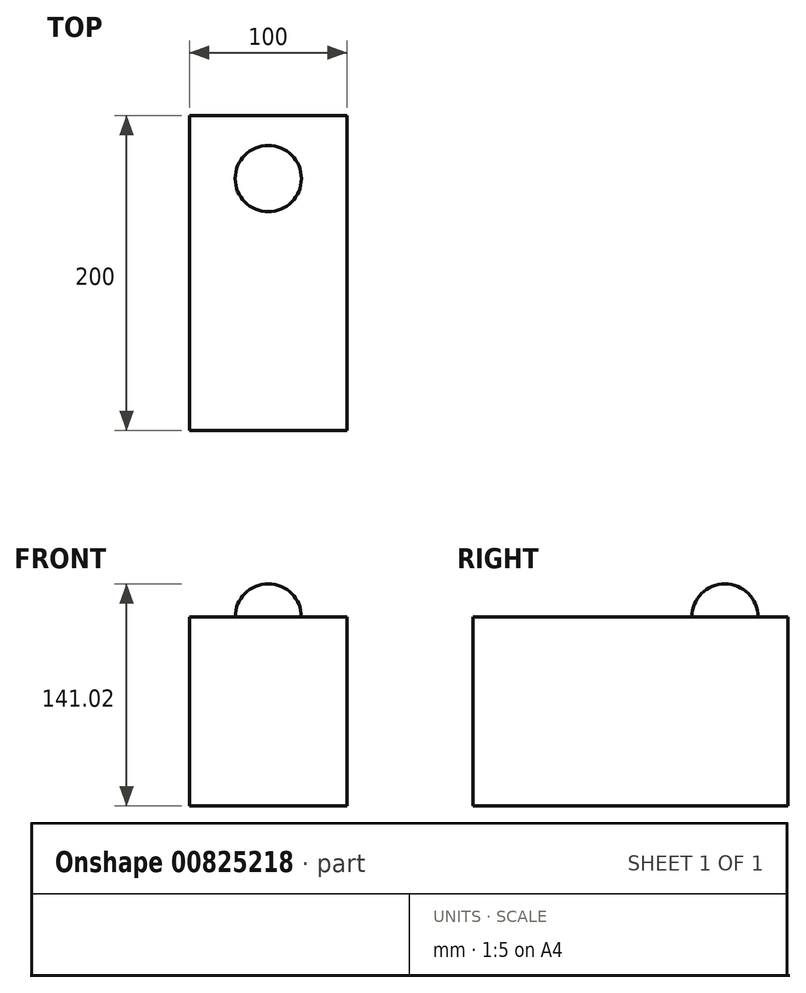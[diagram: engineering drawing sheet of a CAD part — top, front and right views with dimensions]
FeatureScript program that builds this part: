
annotation { "Feature Type Name" : "Feature", "Feature Type Description" : "" }
export const myFeature = defineFeature(function(context is Context, id is Id, definition is map)
    precondition{}
    {
        {
            var Q0;
            Q0=qCreatedBy(makeId("Top.planeOp"),FACE);
            var sketch = newSketch(context, id + "F0", { "sketchPlane" : qUnion([Q0])});
            skLineSegment(sketch, "E0.bottom", {"start": v(50, 100) * mm, "end": v(-50, 100) * mm});
            skLineSegment(sketch, "E0.top", {"start": v(50, -100) * mm, "end": v(-50, -100) * mm});
            skLineSegment(sketch, "E0.left", {"start": v(50, 100) * mm, "end": v(50, -100) * mm});
            skLineSegment(sketch, "E0.right", {"start": v(-50, 100) * mm, "end": v(-50, -100) * mm});
            skPoint(sketch, "E0.middle", {"position": v(0, 0) * mm});
            skSolve(sketch);
        }
        {
            var Q0;
            Q0 = qSketchRegion(id + "F0", true);
            extrude(context, id + "F1", {"entities" : qUnion([Q0]), "depth" : 120 * mm, "offsetDistance" : 25.4 * mm});
        }
        {
            var Q0;
            Q0=makeQuery(id+"F1.opExtrude","CAP_FACE",FACE,{"disambiguationData":[OSD([sQuery(id+"F0.wireOp",EDGE,"E0.bottom"),sQuery(id+"F0.wireOp",EDGE,"E0.top"),sQuery(id+"F0.wireOp",EDGE,"E0.left"),sQuery(id+"F0.wireOp",EDGE,"E0.right")])],"isStart":false});
            var sketch = newSketch(context, id + "F2", { "sketchPlane" : qUnion([Q0])});
            skLineSegment(sketch, "E1", {"start": v(0, -100) * mm, "end": v(0, 100) * mm, "construction": true});
            skArc(sketch, "E2", {"start": v(21.02, 60) * mm, "mid": v(0, 81.02) * mm, "end": v(-21.02, 60) * mm});
            skLineSegment(sketch, "E3", {"start": v(0, 60) * mm, "end": v(-21.02, 60) * mm});
            skLineSegment(sketch, "E4", {"start": v(-21.02, 60) * mm, "end": v(21.02, 60) * mm});
            skSolve(sketch);
        }
        {
            var Q0;
            {var subQ0=sQuery(id+"F2.wireOp",EDGE,"E2");Q0=makeQuery(id+"F2.imprint","IMPRINT",FACE,{"disambiguationData":[TD([[makeQuery(id+"F2.imprint","IMPRINT",EDGE,{"derivedFrom":subQ0}),1.0]])]});}
            var Q1;
            Q1=sQuery(id+"F2.wireOp",EDGE,"E4");
            revolve(context, id + "F3", {"operationType" : NewBodyOperationType.ADD, "surfaceOperationType" : NewSurfaceOperationType.NEW, "entities" : qUnion([Q0]), "axis" : qUnion([Q1]), "revolveType" : RevolveType.FULL});
        }
    });
